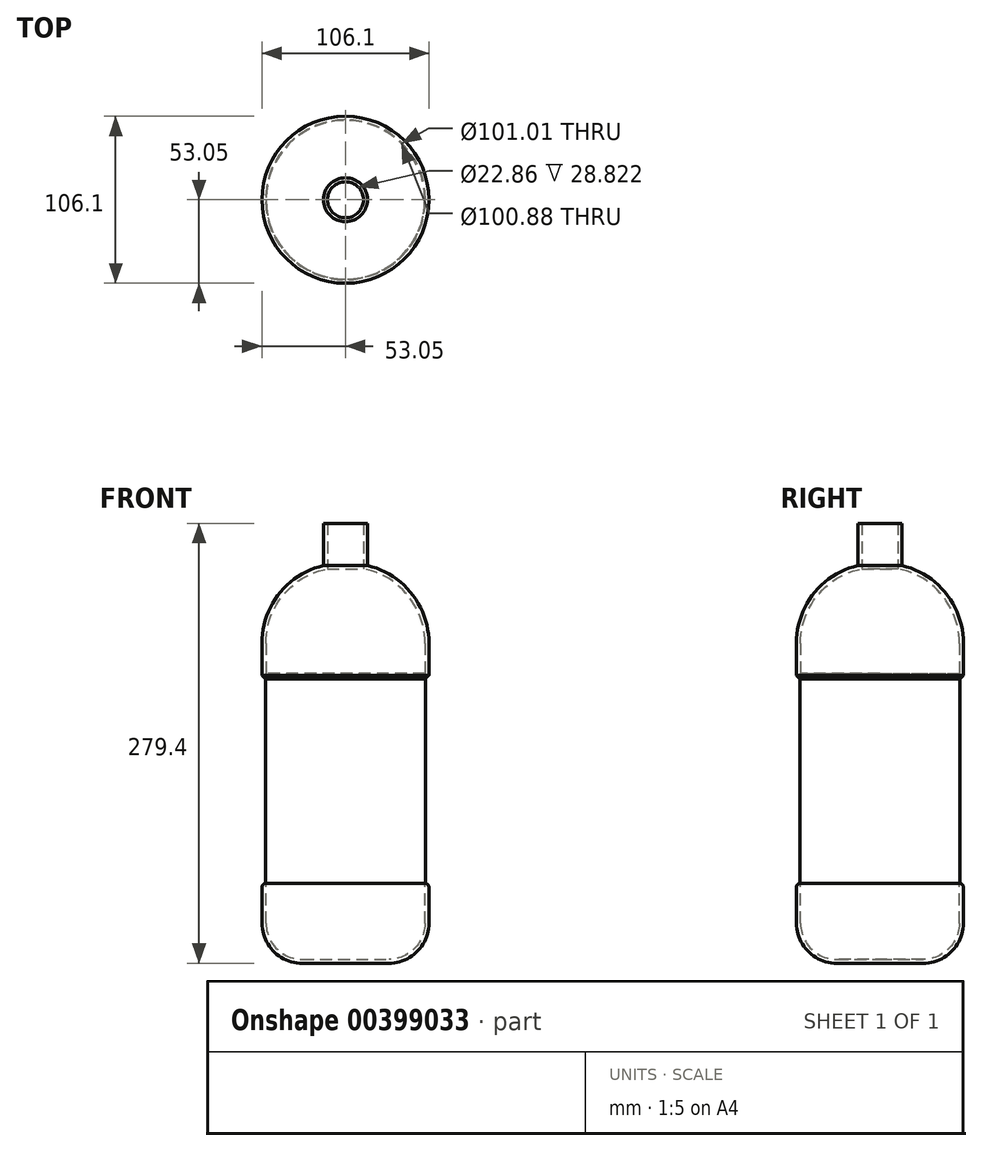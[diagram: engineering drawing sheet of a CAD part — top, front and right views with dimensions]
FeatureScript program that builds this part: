
annotation { "Feature Type Name" : "Feature", "Feature Type Description" : "" }
export const myFeature = defineFeature(function(context is Context, id is Id, definition is map)
    precondition{}
    {
        {
            var Q0;
            Q0=qCreatedBy(makeId("Top.planeOp"),FACE);
            var sketch = newSketch(context, id + "F0", { "sketchPlane" : qUnion([Q0])});
            skCircle(sketch, "E0", {"center": v(0, 0) * mm, "radius": 50.8 * mm});
            skSolve(sketch);
        }
        {
            var Q0;
            Q0 = qSketchRegion(id + "F0", true);
            extrude(context, id + "F1", {"entities" : qUnion([Q0]), "depth" : 127 * mm, "symmetric" : true});
        }
        {
            var Q0;
            Q0=makeQuery(id+"F1.opExtrude","CAP_FACE",FACE,{"disambiguationData":[OSD([sQuery(id+"F0.wireOp",EDGE,"E0")])],"isStart":false});
            var sketch = newSketch(context, id + "F2", { "sketchPlane" : qUnion([Q0])});
            skCircle(sketch, "E1", {"center": v(0, 0) * mm, "radius": 53.05 * mm});
            skSolve(sketch);
        }
        {
            var Q0;
            Q0 = qSketchRegion(id + "F2", true);
            extrude(context, id + "F3", {"entities" : qUnion([Q0]), "operationType" : NewBodyOperationType.ADD, "depth" : 76.2 * mm});
        }
        {
            var Q0;
            Q0=makeQuery(id+"F3.opExtrude","CAP_EDGE",EDGE,{"disambiguationData":[OSD([sQuery(id+"F2.wireOp",EDGE,"E1")])],"isStart":false});
            fillet(context, id + "F4", {"entities" : qUnion([Q0]), "radius" : 50.8 * mm, "tangentPropagation" : true, "allowEdgeOverflow" : false});
        }
        {
            var Q0;
            Q0=makeQuery(id+"F3.opExtrude","CAP_EDGE",EDGE,{"disambiguationData":[OSD([sQuery(id+"F2.wireOp",EDGE,"E1")])],"isStart":true});
            chamfer(context, id + "F5", {"entities" : qUnion([Q0]), "width" : 5.08 * mm, "tangentPropagation" : true});
        }
        {
            var Q0;
            Q0=makeQuery(id+"F3.opExtrude","CAP_FACE",FACE,{"disambiguationData":[OSD([sQuery(id+"F2.wireOp",EDGE,"E1")])],"isStart":false});
            var sketch = newSketch(context, id + "F6", { "sketchPlane" : qUnion([Q0])});
            skCircle(sketch, "E2", {"center": v(0, 0) * mm, "radius": 13.97 * mm});
            skSolve(sketch);
        }
        {
            var Q0;
            Q0 = qSketchRegion(id + "F6", true);
            extrude(context, id + "F7", {"entities" : qUnion([Q0]), "operationType" : NewBodyOperationType.ADD, "depth" : 50.8 * mm, "symmetric" : true});
        }
        {
            var Q0;
            Q0=makeQuery(id+"F1.opExtrude","CAP_FACE",FACE,{"disambiguationData":[OSD([sQuery(id+"F0.wireOp",EDGE,"E0")])],"isStart":true});
            var sketch = newSketch(context, id + "F8", { "sketchPlane" : qUnion([Q0])});
            skCircle(sketch, "E3", {"center": v(0, 0) * mm, "radius": 52.98 * mm});
            skSolve(sketch);
        }
        {
            var Q0;
            Q0 = qSketchRegion(id + "F8", true);
            extrude(context, id + "F9", {"entities" : qUnion([Q0]), "operationType" : NewBodyOperationType.ADD, "depth" : 50.8 * mm});
        }
        {
            var Q0;
            Q0=makeQuery(id+"F9.opExtrude","CAP_EDGE",EDGE,{"disambiguationData":[OSD([sQuery(id+"F8.wireOp",EDGE,"E3")])],"isStart":false});
            fillet(context, id + "F10", {"entities" : qUnion([Q0]), "radius" : 25.4 * mm, "tangentPropagation" : true, "allowEdgeOverflow" : false});
        }
        {
            var Q0;
            Q0=makeQuery(id+"F9.opExtrude","CAP_EDGE",EDGE,{"disambiguationData":[OSD([sQuery(id+"F8.wireOp",EDGE,"E3")])],"isStart":true});
            fillet(context, id + "F11", {"entities" : qUnion([Q0]), "radius" : 2.54 * mm, "tangentPropagation" : true, "allowEdgeOverflow" : false});
        }
        {
            var Q0;
            Q0=makeQuery(id+"F7.opExtrude","CAP_FACE",FACE,{"disambiguationData":[OSD([sQuery(id+"F6.wireOp",EDGE,"E2")])],"isStart":false});
            shell(context, id + "F12", {"entities" : qUnion([Q0]), "thickness" : 2.54 * mm});
        }
    });
